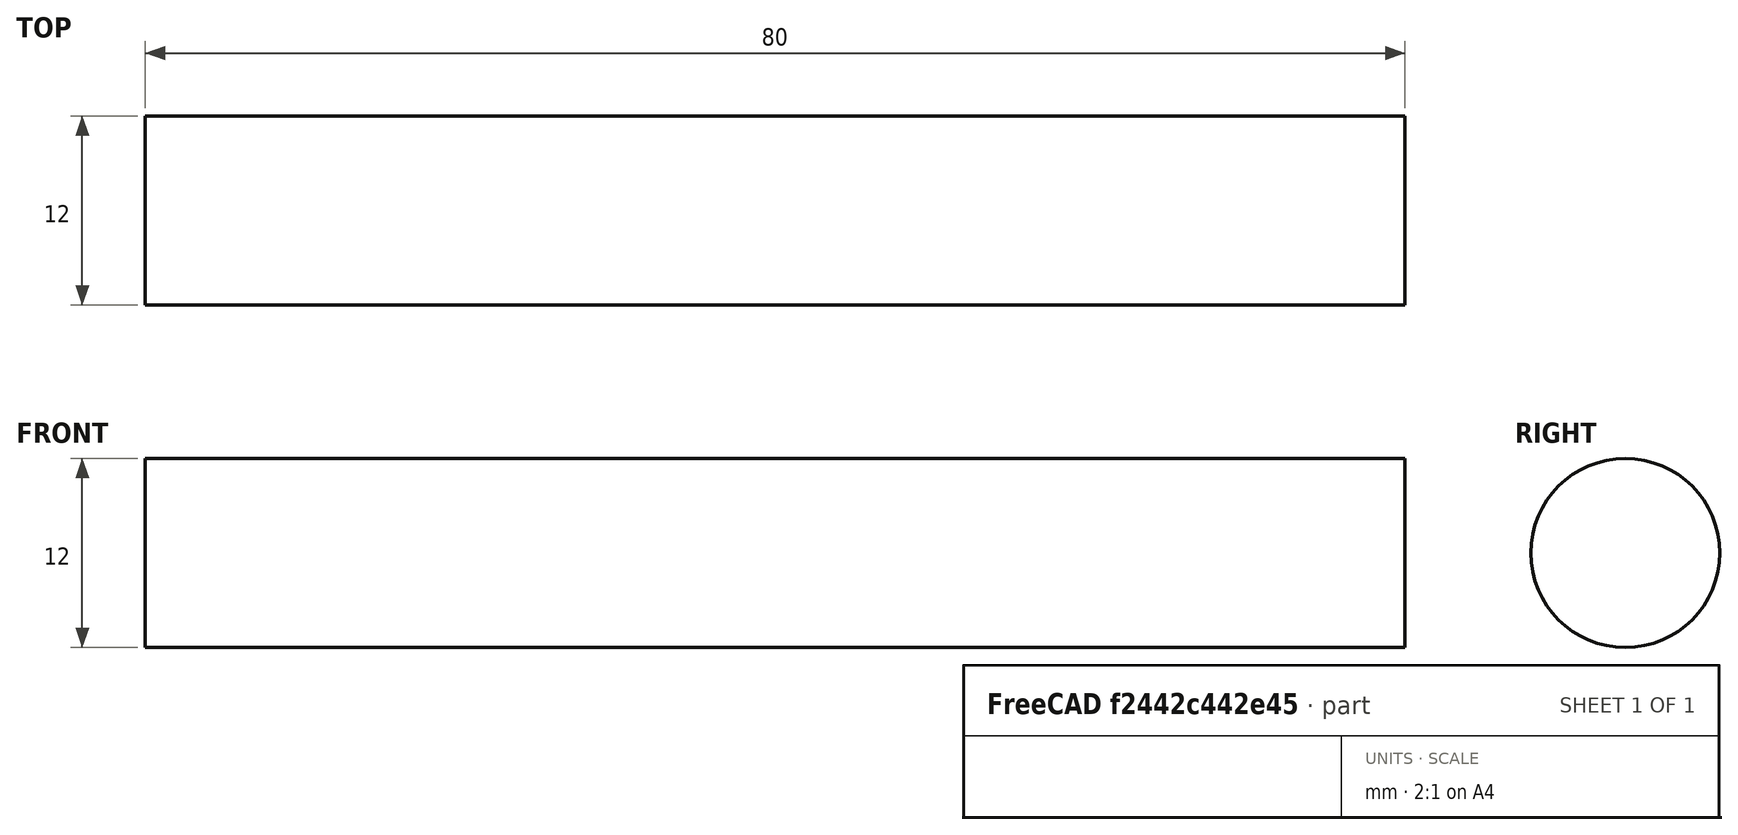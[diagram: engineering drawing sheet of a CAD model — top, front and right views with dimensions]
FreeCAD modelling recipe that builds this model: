
FCSTD DOCUMENT  (FreeCAD 0.19R)
Label: ink
License: All rights reserved
LicenseURL: http://en.wikipedia.org/wiki/All_rights_reserved
objects: Sketcher::SketchObject×1, PartDesign::Revolution×1, PartDesign::Body×1
note: 4 computed .brp shape members not serialized (recipe doc carries the construction recipe); baked Part::Feature solids carry a one-line shape summary decoded from their .brp

FEATURE [Sketcher::SketchObject] Sketch
  MapMode = 5
  Support = -> [XY_Plane]
  sketch-geometry (4):
    g0: LineSegment StartX=0 StartY=0 StartZ=0 EndX=0 EndY=6 EndZ=0
    g1: LineSegment StartX=0 StartY=6 StartZ=0 EndX=80 EndY=6 EndZ=0
    g2: LineSegment StartX=80 StartY=6 StartZ=0 EndX=80 EndY=0 EndZ=0
    g3: LineSegment StartX=80 StartY=0 StartZ=0 EndX=0 EndY=0 EndZ=0
  constraints (11):
    c: Coincident(g0,g-1)
    c: Vertical(g0)
    c: Coincident(g1,g0)
    c: Horizontal(g1)
    c: Coincident(g2,g1)
    c: PointOnObject(g2,g-1)
    c: Vertical(g2)
    c: Coincident(g3,g2)
    c: Coincident(g3,g0)
    c: Distance(g1) = 80
    c: Distance(g0) = 6
FEATURE [PartDesign::Revolution] Revolution
  AllowMultiFace = false
  Angle = 360
  Axis = (1,0,0)
  Base = (0,0,0)
  Profile = -> Sketch
  ReferenceAxis = -> X_Axis
FEATURE [PartDesign::Body] Body
  Group = -> [Sketch,Revolution]
  Origin = -> Origin
  Tip = -> Revolution
